# Revit family: 38122-presto
name_source: partatom
category: Plumbing Fixtures
units: mm (PartAtom-declared; Revit-internal decimal feet)

## family parameters
Always vertical = Yes
Cut with Voids When Loaded = No
Maintain Annotation Orientation = No
OmniClass Number = 23.45.00.00
OmniClass Title = Sanitary, Laundry, and Cleaning Equipment
Part Type = Normal
Room Calculation Point = No
Round Connector Dimension = Use Diameter
Shared = No
Work Plane-Based = Yes

## types (2) — shared parameters
- Hydraulic supply = 20.00 mm
Default Elevation = 1219 mm
Recommended pressure = 3.0 bar
flow = 8.0 L/min
flow time = 30.0 s
material 1 = Default New Material
material1 = Chromed brass.
min pressure = 1.0 bar
pressure = 5.0 bar

## per-type parameters (varying)
| type | Description | Model | URL | brand | range | ref |
| 60380 |  |  |  |  |  |  |
| 38122- Les Robinets PRESTO | 1 Flat gasket
1 Filter gasket
2 Union nuts 3/4" (20x27) for 14x16 mm tube
1 Rosace de finition pour montage sur panneau | 38122 | https://www.prestodatashare.com | Les Robinets PRESTO | Single tap for shower | 38122 - PRESTO 50 PANEL |

## geometry (parser evidence)
native form markers: Sweep x2
no freeform markers — native parametric forms only
